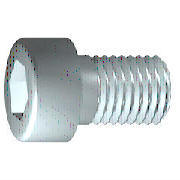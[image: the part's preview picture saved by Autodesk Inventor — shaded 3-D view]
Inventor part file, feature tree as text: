
AUTODESK INVENTOR PART (.ipt)
format: ipt  version: 2020 (Build 240168000, 168)  size: 185,856 bytes
history: native  units: mm (DEFAULTED — no unit token found)
features: sketch x2, other x1, extrude x1, plane x1, fillet x1
ambient origin geometry x7: Origin, YZ Plane, XY Plane, X Axis, Y Axis, Z Axis, Center Point
bodies: Solid1 (feature_tree)
feature tree (6):
  other  "Bryła"
  extrude  "Szczelina"  Depth=24.0mm
  plane  "Work Plane1"
  fillet  "Fillet2"  Radius=0.61355mm
  sketch  "Szkic1"
  sketch  "Szkic2"
